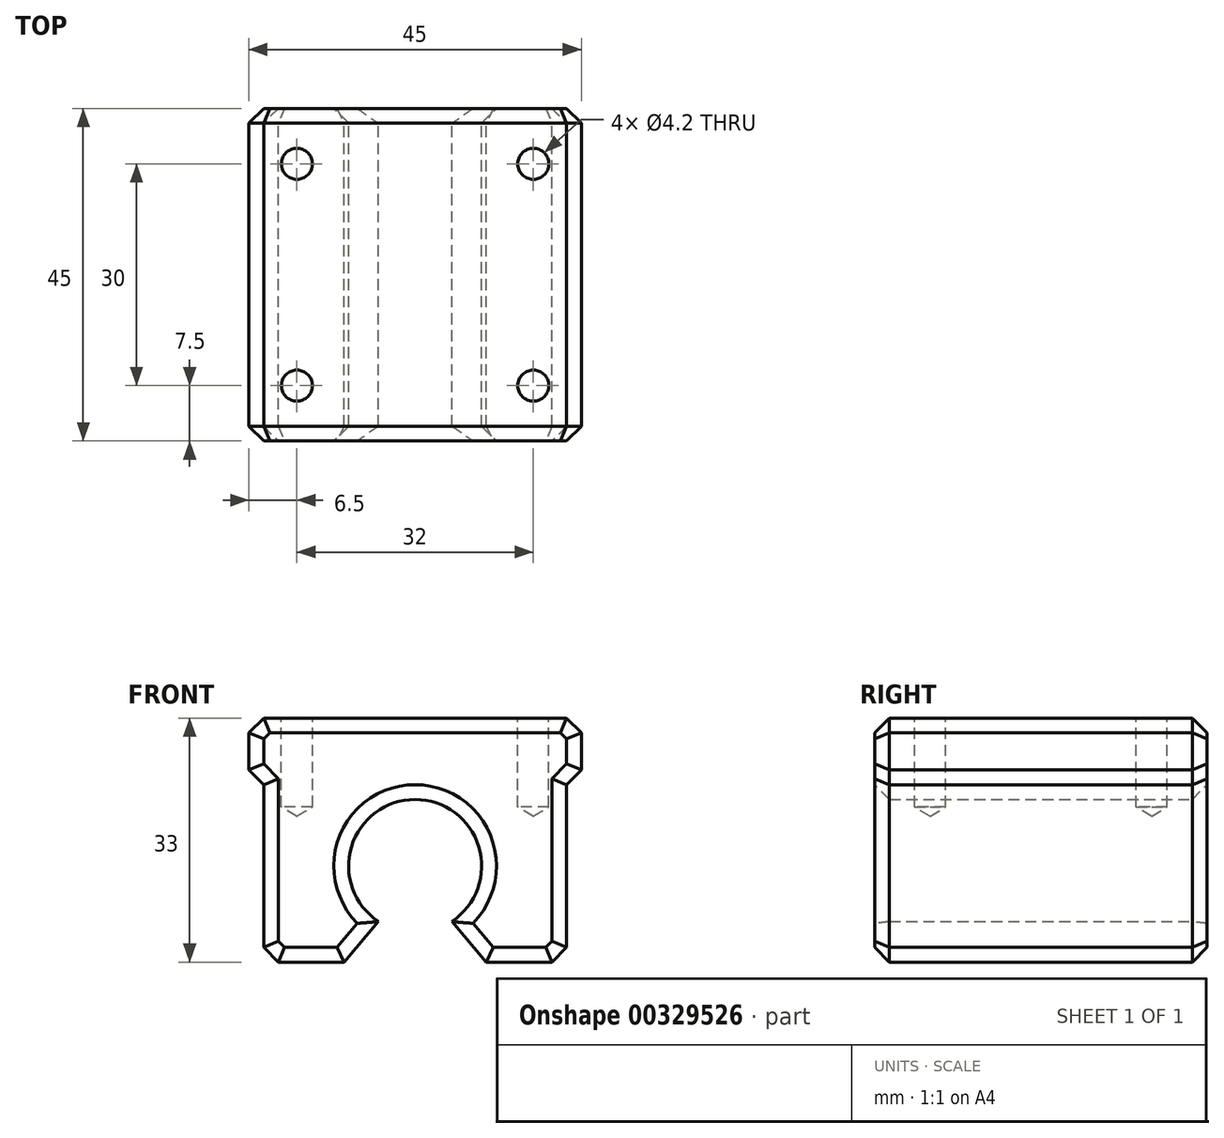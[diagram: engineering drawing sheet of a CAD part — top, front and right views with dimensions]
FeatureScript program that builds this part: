
annotation { "Feature Type Name" : "Feature", "Feature Type Description" : "" }
export const myFeature = defineFeature(function(context is Context, id is Id, definition is map)
    precondition{}
    {
        {
            var Q0;
            Q0=qCreatedBy(makeId("Front.planeOp"),FACE);
            var sketch = newSketch(context, id + "F0", { "sketchPlane" : qUnion([Q0])});
            skArc(sketch, "E0", {"start": v(5, -7.49) * mm, "mid": v(0, 9) * mm, "end": v(-5, -7.49) * mm});
            skLineSegment(sketch, "E1", {"start": v(5, -7.49) * mm, "end": v(9.62, -13) * mm});
            skLineSegment(sketch, "E2", {"start": v(9.62, -13) * mm, "end": v(18.5, -13) * mm});
            skLineSegment(sketch, "E3", {"start": v(18.5, -13) * mm, "end": v(20.5, -11) * mm});
            skLineSegment(sketch, "E4", {"start": v(20.5, -11) * mm, "end": v(20.5, 11) * mm});
            skLineSegment(sketch, "E5", {"start": v(20.5, 11) * mm, "end": v(22.5, 13) * mm});
            skLineSegment(sketch, "E6", {"start": v(22.5, 13) * mm, "end": v(22.5, 18) * mm});
            skLineSegment(sketch, "E7", {"start": v(22.5, 18) * mm, "end": v(20.5, 20) * mm});
            skLineSegment(sketch, "E8", {"start": v(20.5, 20) * mm, "end": v(-20.5, 20) * mm});
            skLineSegment(sketch, "E9", {"start": v(-20.5, 20) * mm, "end": v(-22.5, 18) * mm});
            skLineSegment(sketch, "E10", {"start": v(-20.5, 11) * mm, "end": v(-20.5, -11) * mm});
            skLineSegment(sketch, "E11", {"start": v(-20.5, -11) * mm, "end": v(-18.5, -13) * mm});
            skLineSegment(sketch, "E12", {"start": v(-18.5, -13) * mm, "end": v(-9.62, -13) * mm});
            skLineSegment(sketch, "E13", {"start": v(-9.62, -13) * mm, "end": v(-5, -7.49) * mm});
            skLineSegment(sketch, "E14", {"start": v(-22.5, 18) * mm, "end": v(-22.5, 13) * mm});
            skLineSegment(sketch, "E15", {"start": v(-22.5, 13) * mm, "end": v(-20.5, 11) * mm});
            skPoint(sketch, "E16", {"position": v(0, 20) * mm});
            skLineSegment(sketch, "E17", {"start": v(-9.62, -13) * mm, "end": v(9.62, -13) * mm, "construction": true});
            skPoint(sketch, "E18", {"position": v(0, -13) * mm});
            skSolve(sketch);
        }
        {
            var Q0;
            Q0 = qSketchRegion(id + "F0", true);
            extrude(context, id + "F1", {"entities" : qUnion([Q0]), "endBound" : BoundingType.SYMMETRIC, "depth" : 45 * mm});
        }
        {
            var Q0;
            Q0=makeQuery(id+"F1.opExtrude","CAP_FACE",FACE,{"disambiguationData":[OSD([sQuery(id+"F0.wireOp",EDGE,"E0"),sQuery(id+"F0.wireOp",EDGE,"E1"),sQuery(id+"F0.wireOp",EDGE,"E2"),sQuery(id+"F0.wireOp",EDGE,"E3"),sQuery(id+"F0.wireOp",EDGE,"E4"),sQuery(id+"F0.wireOp",EDGE,"E5"),sQuery(id+"F0.wireOp",EDGE,"E6"),sQuery(id+"F0.wireOp",EDGE,"E7"),sQuery(id+"F0.wireOp",EDGE,"E8"),sQuery(id+"F0.wireOp",EDGE,"E9"),sQuery(id+"F0.wireOp",EDGE,"E10"),sQuery(id+"F0.wireOp",EDGE,"E11"),sQuery(id+"F0.wireOp",EDGE,"E12"),sQuery(id+"F0.wireOp",EDGE,"E13"),sQuery(id+"F0.wireOp",EDGE,"E14"),sQuery(id+"F0.wireOp",EDGE,"E15")])],"isStart":false});
            var Q1;
            Q1=makeQuery(id+"F1.opExtrude","CAP_FACE",FACE,{"disambiguationData":[OSD([sQuery(id+"F0.wireOp",EDGE,"E0"),sQuery(id+"F0.wireOp",EDGE,"E1"),sQuery(id+"F0.wireOp",EDGE,"E2"),sQuery(id+"F0.wireOp",EDGE,"E3"),sQuery(id+"F0.wireOp",EDGE,"E4"),sQuery(id+"F0.wireOp",EDGE,"E5"),sQuery(id+"F0.wireOp",EDGE,"E6"),sQuery(id+"F0.wireOp",EDGE,"E7"),sQuery(id+"F0.wireOp",EDGE,"E8"),sQuery(id+"F0.wireOp",EDGE,"E9"),sQuery(id+"F0.wireOp",EDGE,"E10"),sQuery(id+"F0.wireOp",EDGE,"E11"),sQuery(id+"F0.wireOp",EDGE,"E12"),sQuery(id+"F0.wireOp",EDGE,"E13"),sQuery(id+"F0.wireOp",EDGE,"E14"),sQuery(id+"F0.wireOp",EDGE,"E15")])],"isStart":true});
            chamfer(context, id + "F2", {"entities" : qUnion([Q0, Q1]), "width" : 2 * mm, "tangentPropagation" : true});
        }
        {
            var Q0;
            Q0=makeQuery(id+"F1.opExtrude","SWEPT_FACE",FACE,{"disambiguationData":[OSD([sQuery(id+"F0.wireOp",EDGE,"E8")])]});
            var sketch = newSketch(context, id + "F3", { "sketchPlane" : qUnion([Q0])});
            skPoint(sketch, "E19", {"position": v(-16, 15) * mm});
            skPoint(sketch, "E20", {"position": v(-16, -15) * mm});
            skPoint(sketch, "E21", {"position": v(16, 15) * mm});
            skPoint(sketch, "E22", {"position": v(16, -15) * mm});
            skSolve(sketch);
        }
        {
            var Q0;
            Q0=sQuery(id+"F3.wireOp",VERTEX,"E19");
            var Q1;
            Q1=sQuery(id+"F3.wireOp",VERTEX,"E21");
            var Q2;
            Q2=sQuery(id+"F3.wireOp",VERTEX,"E22");
            var Q3;
            Q3=sQuery(id+"F3.wireOp",VERTEX,"E20");
            var Q4;
            Q4=makeQuery(id+"F1.opExtrude","SWEPT_BODY",BODY,{"disambiguationData":[OSD([sQuery(id+"F0.wireOp",EDGE,"E0"),sQuery(id+"F0.wireOp",EDGE,"E1"),sQuery(id+"F0.wireOp",EDGE,"E2"),sQuery(id+"F0.wireOp",EDGE,"E3"),sQuery(id+"F0.wireOp",EDGE,"E4"),sQuery(id+"F0.wireOp",EDGE,"E5"),sQuery(id+"F0.wireOp",EDGE,"E6"),sQuery(id+"F0.wireOp",EDGE,"E7"),sQuery(id+"F0.wireOp",EDGE,"E8"),sQuery(id+"F0.wireOp",EDGE,"E9"),sQuery(id+"F0.wireOp",EDGE,"E10"),sQuery(id+"F0.wireOp",EDGE,"E11"),sQuery(id+"F0.wireOp",EDGE,"E12"),sQuery(id+"F0.wireOp",EDGE,"E13"),sQuery(id+"F0.wireOp",EDGE,"E14"),sQuery(id+"F0.wireOp",EDGE,"E15")])]});
            hole(context, id + "F4", {"style" : HoleStyle.SIMPLE, "endStyle" : HoleEndStyle.BLIND, "standardTappedOrClearance" : lookupTablePath({ "standard" : "ISO", "engagement" : "75%", "pitch" : "0.8 mm", "size" : "M5", "type" : "Tapped" }), "standardBlindInLast" : lookupTablePath({ "standard" : "ISO", "engagement" : "75%", "pitch" : "0.8 mm", "size" : "M5", "type" : "Tapped" }), "holeDiameter" : 4.2 * mm, "showTappedDepth" : true, "holeDepth" : 12 * mm, "tappedDepth" : 9.6 * mm, "tapClearance" : 3, "locations" : qUnion([Q0, Q1, Q2, Q3]), "scope" : qUnion([Q4]), "majorDiameter" : 5 * mm});
        }
    });
